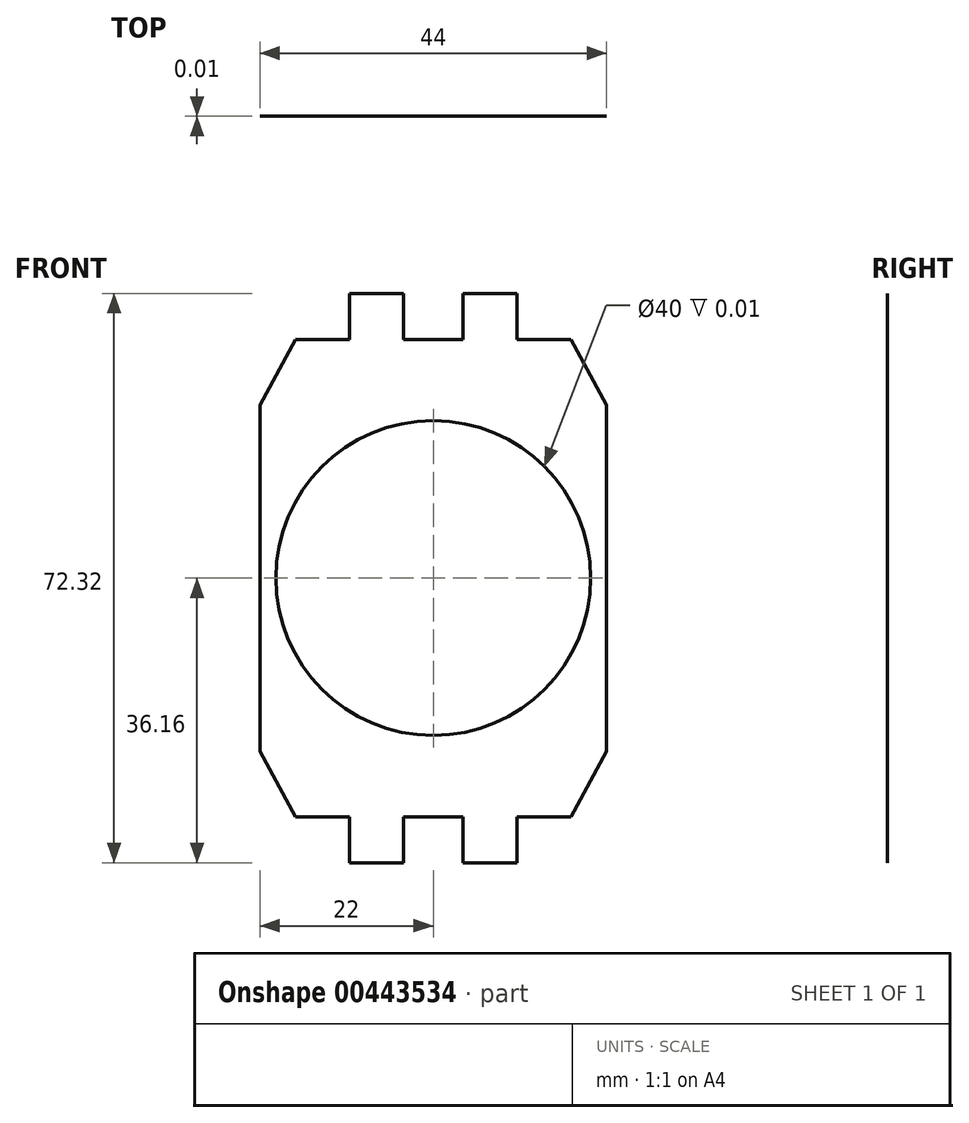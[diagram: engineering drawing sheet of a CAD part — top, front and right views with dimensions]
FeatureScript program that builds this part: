
annotation { "Feature Type Name" : "Feature", "Feature Type Description" : "" }
export const myFeature = defineFeature(function(context is Context, id is Id, definition is map)
    precondition{}
    {
        {
            var Q0;
            Q0=qCreatedBy(makeId("Front.planeOp"),FACE);
            var sketch = newSketch(context, id + "F0", { "sketchPlane" : qUnion([Q0])});
            skCircle(sketch, "E0", {"center": v(0, 0) * mm, "radius": 20 * mm});
            skLineSegment(sketch, "E1.bottom", {"start": v(-17.5, 30.31) * mm, "end": v(17.5, 30.31) * mm});
            skLineSegment(sketch, "E1.top", {"start": v(-17.5, -30.31) * mm, "end": v(17.5, -30.31) * mm});
            skLineSegment(sketch, "E1.left", {"start": v(-17.5, 30.31) * mm, "end": v(-17.5, -30.31) * mm});
            skLineSegment(sketch, "E1.right", {"start": v(17.5, 30.31) * mm, "end": v(17.5, -30.31) * mm});
            skPoint(sketch, "E2", {"position": v(-17.5, 0) * mm});
            skPoint(sketch, "E3", {"position": v(17.5, 0) * mm});
            skLineSegment(sketch, "E4.bottom", {"start": v(-22, 22) * mm, "end": v(22, 22) * mm});
            skLineSegment(sketch, "E4.top", {"start": v(-22, -22) * mm, "end": v(22, -22) * mm});
            skLineSegment(sketch, "E4.left", {"start": v(-22, 22) * mm, "end": v(-22, -22) * mm});
            skLineSegment(sketch, "E4.right", {"start": v(22, 22) * mm, "end": v(22, -22) * mm});
            skPoint(sketch, "E5", {"position": v(-22, 0) * mm});
            skPoint(sketch, "E6", {"position": v(22, 0) * mm});
            skLineSegment(sketch, "E7", {"start": v(-22, 22) * mm, "end": v(-17.5, 30.31) * mm});
            skLineSegment(sketch, "E8", {"start": v(-22, -22) * mm, "end": v(-17.5, -30.31) * mm});
            skLineSegment(sketch, "E9", {"start": v(17.5, -30.31) * mm, "end": v(22, -22) * mm});
            skLineSegment(sketch, "E10", {"start": v(22, 22) * mm, "end": v(17.5, 30.31) * mm});
            skSolve(sketch);
        }
        {
            var Q0;
            Q0 = qSketchRegion(id + "F0", true);
            var Q1;
            {var subQ0=sQuery(id+"F0.wireOp",EDGE,"E1.left");var subQ1=sQuery(id+"F0.wireOp",EDGE,"E0");var subQ2=makeQuery(id+"F0.imprint","INTERSECT",VERTEX,{"disambiguationData":[OD(0.0)],"derivedFrom":[subQ1,subQ0]});Q1=makeQuery(id+"F0.imprint","IMPRINT",FACE,{"disambiguationData":[TD([[makeQuery(id+"F0.imprint","IMPRINT",EDGE,{"disambiguationData":[TD([[subQ2,1.0]])],"derivedFrom":subQ1}),-1.0]])]});}
            var Q2;
            {var subQ0=sQuery(id+"F0.wireOp",EDGE,"E1.left");var subQ1=sQuery(id+"F0.wireOp",EDGE,"E0");var subQ2=makeQuery(id+"F0.imprint","INTERSECT",VERTEX,{"disambiguationData":[OD(1.0)],"derivedFrom":[subQ1,subQ0]});Q2=makeQuery(id+"F0.imprint","IMPRINT",FACE,{"disambiguationData":[TD([[makeQuery(id+"F0.imprint","IMPRINT",EDGE,{"disambiguationData":[TD([[subQ2,-1.0]])],"derivedFrom":subQ1}),-1.0]])]});}
            extrude(context, id + "F1", {"entities" : qUnion([Q0, Q1, Q2]), "depth" : 1 / 101.6 * mm});
        }
        {
            var Q0;
            Q0=makeQuery(id+"F1.opExtrude","CAP_FACE",FACE,{"disambiguationData":[OSD([sQuery(id+"F0.wireOp",EDGE,"E0"),sQuery(id+"F0.wireOp",EDGE,"E1.bottom"),sQuery(id+"F0.wireOp",EDGE,"E1.top"),sQuery(id+"F0.wireOp",EDGE,"E4.left"),sQuery(id+"F0.wireOp",EDGE,"E4.right"),sQuery(id+"F0.wireOp",EDGE,"E7"),sQuery(id+"F0.wireOp",EDGE,"E8"),sQuery(id+"F0.wireOp",EDGE,"E9"),sQuery(id+"F0.wireOp",EDGE,"E10")])],"isStart":false});
            var sketch = newSketch(context, id + "F2", { "sketchPlane" : qUnion([Q0])});
            skLineSegment(sketch, "E11.bottom", {"start": v(-10.65, 30.31) * mm, "end": v(-3.75, 30.31) * mm});
            skLineSegment(sketch, "E11.top", {"start": v(-10.65, 36.16) * mm, "end": v(-3.75, 36.16) * mm});
            skLineSegment(sketch, "E11.left", {"start": v(-10.65, 30.31) * mm, "end": v(-10.65, 36.16) * mm});
            skLineSegment(sketch, "E11.right", {"start": v(-3.75, 30.31) * mm, "end": v(-3.75, 36.16) * mm});
            skLineSegment(sketch, "E12.bottom", {"start": v(3.75, 30.31) * mm, "end": v(10.65, 30.31) * mm});
            skLineSegment(sketch, "E12.top", {"start": v(3.75, 36.16) * mm, "end": v(10.65, 36.16) * mm});
            skLineSegment(sketch, "E12.left", {"start": v(3.75, 30.31) * mm, "end": v(3.75, 36.16) * mm});
            skLineSegment(sketch, "E12.right", {"start": v(10.65, 30.31) * mm, "end": v(10.65, 36.16) * mm});
            skLineSegment(sketch, "E13.bottom", {"start": v(-10.65, -30.31) * mm, "end": v(-3.75, -30.31) * mm});
            skLineSegment(sketch, "E13.top", {"start": v(-10.65, -36.16) * mm, "end": v(-3.75, -36.16) * mm});
            skLineSegment(sketch, "E13.left", {"start": v(-10.65, -30.31) * mm, "end": v(-10.65, -36.16) * mm});
            skLineSegment(sketch, "E13.right", {"start": v(-3.75, -30.31) * mm, "end": v(-3.75, -36.16) * mm});
            skLineSegment(sketch, "E14.bottom", {"start": v(3.75, -30.31) * mm, "end": v(10.65, -30.31) * mm});
            skLineSegment(sketch, "E14.top", {"start": v(3.75, -36.16) * mm, "end": v(10.65, -36.16) * mm});
            skLineSegment(sketch, "E14.left", {"start": v(3.75, -30.31) * mm, "end": v(3.75, -36.16) * mm});
            skLineSegment(sketch, "E14.right", {"start": v(10.65, -30.31) * mm, "end": v(10.65, -36.16) * mm});
            skPoint(sketch, "E15", {"position": v(0, 30.31) * mm});
            skPoint(sketch, "E16", {"position": v(0, -30.31) * mm});
            skSolve(sketch);
        }
        {
            var Q0;
            Q0 = qSketchRegion(id + "F2", true);
            extrude(context, id + "F3", {"entities" : qUnion([Q0]), "operationType" : NewBodyOperationType.ADD, "oppositeDirection" : true, "depth" : 1 / 101.6 * mm});
        }
    });
